FCSTD DOCUMENT  (FreeCAD 0.21R33771 (Git))
Label: our projectnew
License: All rights reserved
LicenseURL: http://en.wikipedia.org/wiki/All_rights_reserved
objects: Sketcher::SketchObject×1, PartDesign::Body×1
note: 2 computed .brp shape members not serialized (recipe doc carries the construction recipe); baked Part::Feature solids carry a one-line shape summary decoded from their .brp

FEATURE [Sketcher::SketchObject] Sketch
  FullyConstrained = false
  MapMode = 5
  Placement = pos=(0,0,0) rot=(0.57735,0.57735,0.57735;2.0944rad)
  Support = -> [YZ_Plane]
  sketch-geometry (14):
    g0: LineSegment StartX=229.404 StartY=474.788 StartZ=0 EndX=-470.596 EndY=474.788 EndZ=0
    g1: LineSegment StartX=-470.596 StartY=474.788 StartZ=0 EndX=-470.596 EndY=463.674 EndZ=0
    g2: LineSegment StartX=-470.596 StartY=463.674 StartZ=0 EndX=-470.596 EndY=613.674 EndZ=0
    g3: LineSegment StartX=-470.596 StartY=613.674 StartZ=0 EndX=-799.134 EndY=810.937 EndZ=0
    g4: LineSegment StartX=-799.134 StartY=810.937 StartZ=0 EndX=-703.028 EndY=974.954 EndZ=0
    g5: LineSegment StartX=-703.028 StartY=974.954 StartZ=0 EndX=-603.623 EndY=908.055 EndZ=0
    g6: LineSegment StartX=-603.623 StartY=908.055 StartZ=0 EndX=96.3768 EndY=908.055 EndZ=0
    g7: LineSegment StartX=96.3768 StartY=908.055 StartZ=0 EndX=401.617 EndY=1033.84 EndZ=0
    g8: LineSegment StartX=401.617 StartY=1033.84 StartZ=0 EndX=401.617 EndY=892.857 EndZ=0
    g9: LineSegment StartX=401.617 StartY=892.857 StartZ=0 EndX=229.404 EndY=774.788 EndZ=0
    g10: LineSegment StartX=229.404 StartY=774.788 StartZ=0 EndX=229.404 EndY=474.788 EndZ=0
    g11: GeomPoint X=-557.754 Y=947.312 Z=0
    g12: LineSegment StartX=497.259 StartY=1032.9 StartZ=0 EndX=497.259 EndY=455.882 EndZ=0
    g13: LineSegment StartX=401.095 StartY=374.575 StartZ=0 EndX=-858.295 EndY=374.575 EndZ=0
  constraints (32):
    c: Horizontal(g0)
    c: Coincident(g0,g1)
    c: Vertical(g1)
    c: Coincident(g1,g2)
    c: Vertical(g2)
    c: Coincident(g2,g3)
    c: Coincident(g3,g4)
    c: Coincident(g4,g5)
    c: Coincident(g5,g6)
    c: Horizontal(g6)
    c: Coincident(g6,g7)
    c: Coincident(g7,g8)
    c: Vertical(g8)
    c: Coincident(g8,g9)
    c: Coincident(g9,g10)
    c: Coincident(g10,g0)
    c: Vertical(g10)
    c: DistanceX(g0,g0) = 700
    c: DistanceY(g2,g2) = 150
    c: DistanceY(g10,g10) = 300
    c: Distance(g3) = 383.21
    c: Distance(g4) = 190.1
    c: Distance(g5) = 119.82
    c: DistanceX(g6,g6) = 700
    c: DistanceX(g7,g7) = 305.24
    c: Distance(g7) = 330.14
    c: DistanceY(g8,g8) = 140.98
    c: Distance(g9) = 208.8
    c: Vertical(g12)
    c: DistanceY(g12,g12) = 577.02
    c: Horizontal(g13)
    c: DistanceX(g13,g13) = 1259.39
FEATURE [PartDesign::Body] Body
  Group = -> [Sketch]
  Origin = -> Origin
